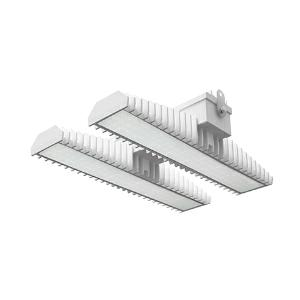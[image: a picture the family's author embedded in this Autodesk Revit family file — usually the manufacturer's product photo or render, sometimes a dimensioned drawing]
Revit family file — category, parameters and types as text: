
# Revit family: 3f_filippi_-_3f_lem_ho_ampio_3f_filippi_-_58954_a0812_-_3f_lem_2_ho_led_140_cr_ampio___vs_5d09
name_source: partatom
category: Lighting Fixtures
units: mm (PartAtom-declared; Revit-internal decimal feet)

## family parameters
Cut with Voids When Loaded = No
Host = Face
Light Source = No
Part Type = Normal
Room Calculation Point = No
Round Connector Dimension = Use Diameter
Shared = No

## types (1)
- 3F Filippi - 3F LEM HO Ampio (1 x LED, 17702 lm, 138 W, 4000 K)
    Apparent Load = 138 VA
    Approval mark = CE
    CIE Flux Codes = 67 90 97 100 100
    Color Rendering = 80
    Color Temperature = 4000 K
    Control Gear = Electronic ballast
    Default Elevation = 1800 mm
    Description = Industrial luminaire with high light output and high luminous efficiency designed with the most innovative technologies for environments with temperature up to 55°C.

ILLUMINOTECHNICAL
Luminous efficiency 100% (DLOR 98%, ULOR 2%).
Initial luminous flux of the luminaire 17702 lm.
Direct symmetric wide distribution: the illuminated area has a rectangular shape.
Installation Interdistance Transv.D = 1.24 x hu - Long.D = 1.20 x hu.
Tabular UGR (CIE 117 - 4H-8H; S=0.25H; 70/50/20): RUG 23.1 - 23.1.
Beam angle: 82° - 83°.
Luminous efficacy 128 lm/W.
Lifetime (L93/B10): 30000 h. (tq+25°C)
Lifetime (L90/B10): 50000 h. (tq+25°C)
Lifetime (L85/B10): 80000 h. (tq+25°C)
Lifetime (L80/B10): 100000 h. (tq+25°C)
Lifetime (L85/B10): 50000 h. (tq+55°C)
Sudden decreased luminous flux after 50000 hours: 0% (C0).
Photobiological safety in compliance with IEC/TR 62778: RG0 risk exempt, (IEC 62471).
In compliance with IEC/EN 62722-2-1 - IEC/EN 62717 standards.

SOURCE
2 Mid-Power linear LED modules 70W/840.
Energy efficiency class (UE 2019/2020 - UE 2019/2015): C.
CIE 13.3 Colour rendering index: CRI >80 (R9 <50%).
IES TM-30 Fidelity Index: Rf = 84 Rg = 95.
CCT nominal colour temperature 4000 K.
Colour initial tolerance (MacAdam): SDCM 3.

MECHANICAL
Passive modular heatsinks in die-casted aluminium, painted in white colour.
To optimize the thermal management of the LED module, the heatsinks are oversized and provided with self-cleaning of cooling fins.
Wiring body in aluminium and galvanised steel anchored solidly to the sinks and thermally separated.
3F Lens lenses with high luminous efficiency, transparent methacrylate (PMMA), fixed to the LED modules.
Fixing brackets in stainless steel.
Luminaire with limited surface temperature. - D - (EN 60598-2-24)
Dimensions: 470x542 mm, height 133 mm. Weight 10.135 kg.
IP65 protection degree.
Mechanical strength to impacts IK06 (1 joule).
Glow-wire test resistance 650°C.

ELECTRICAL
Halogen Free electronic wiring 230V-50/60Hz, power factor 0.97, THD <25%, constant output current, class I, 1 driver.
Power of the luminaire 138 W.
ENEC - CE.
SAFE FLICKER: PstLM=<1 and SVM=<0.4 (IEC TR 61547-1 and IEC TR 63158), to ensure a more comfortable and safe light.
Luminaire compliant with EN 60598-2-22 for power supply from a centralised emergency system CPSS (Central Power Supply System), not incorporated in the luminaire - high risk areas excluded. The default power and flux are 100% in AC and 100% in DC.
Ambient temperature from -30°C to +55°C.
Temperature class T6 max 85°C.
Quick connection via M20 3P connector with 9-13 mm tightening range.
Power unit positioned on a separate compartment by the LED module to ensure optimum temperatures of cabling components, to be inspectable and maintainable.
Relative humidity UR: <85%.

INSTALLATION
Ceiling / Suspended / Wall.
All accessories dedicated to this product are available on the Catalog and on our website www.3F-Filippi.com.

ACCESSORIES
A0812 - Anti-glare microprismatic VS moulded glass, tempered, not flammable, with sealing gasket.
One required for each light module. The pack contains 10 pieces.

APPLICATIONS
In commercial environments, exhibition and industrial areas, stores, open areas.
Environments in which it is necessary a total protection against falling fragments (eg environments with foodstuffs or machines with moving parts or with extreme temperature changes), use luminaires with polycarbonate lenses.

WARNING
Fixture not suitable for cold stores with an ambient temperature <0°C and/or relative humidity >85%.
Luminaire designed for disposal/recycling at end-of-life.
Replaceable (LED only) light source by a professional. Replaceable control gear by a professional.
    Height = 133 mm  [stored 0.436352 ft]
    Lamp = 1 x LED
    Lamp Light Flux = 17702 lm
    Lamp Power = 138 W
    Lamp count = 1
    Length = 470 mm
    Lifetime = 50000 h
    Luminous efficacy = 128 lm/W
    Manufacturer = 3F Filippi
    ModVariant = No
    Model = 3F Filippi - 58954+A0812 - 3F LEM 2 HO LED 140 CR AMPIO + VS
    Mounting Place = Ceiling
    Mounting Type = Pendant
    Number of Poles = 1
    OnlyDefault = Yes
    Power Factor = 1
    Product Name = 3F Filippi - 3F LEM HO Ampio
    Product group = pendant luminaire
    ProductGroupID = 9
    Protection Class = Protection class I
    Protection Degree = IP 65
    RLX_Detail_Level = 1
    RLX_Emergency_Light_Flux = 0 lm
    RLX_Emergency_Type = 0
    RLX_Emergency_Type_DB = No
    RlxData = <blob elided: 95301 chars, md5=51196a0c>
    Socket = socket
    Standby Power = 0 W
    System Light Flux = 17702 lm
    System Power = 138 W
    Type Comments = Product without accessories
    Type Image = 3f_filippi_-_lem_2__a0812.jpg
    URL = http://relux.com
    VarID = ---
    Voltage = 0 V
    Weight = 0.00 kg
    Width = 542 mm

note: [stored X ft] marks values corroborated as IEEE doubles in the binary element streams (Revit-internal decimal feet)

## geometry (parser evidence)
native form markers: Blend x4, Sweep x11
no freeform markers — native parametric forms only
